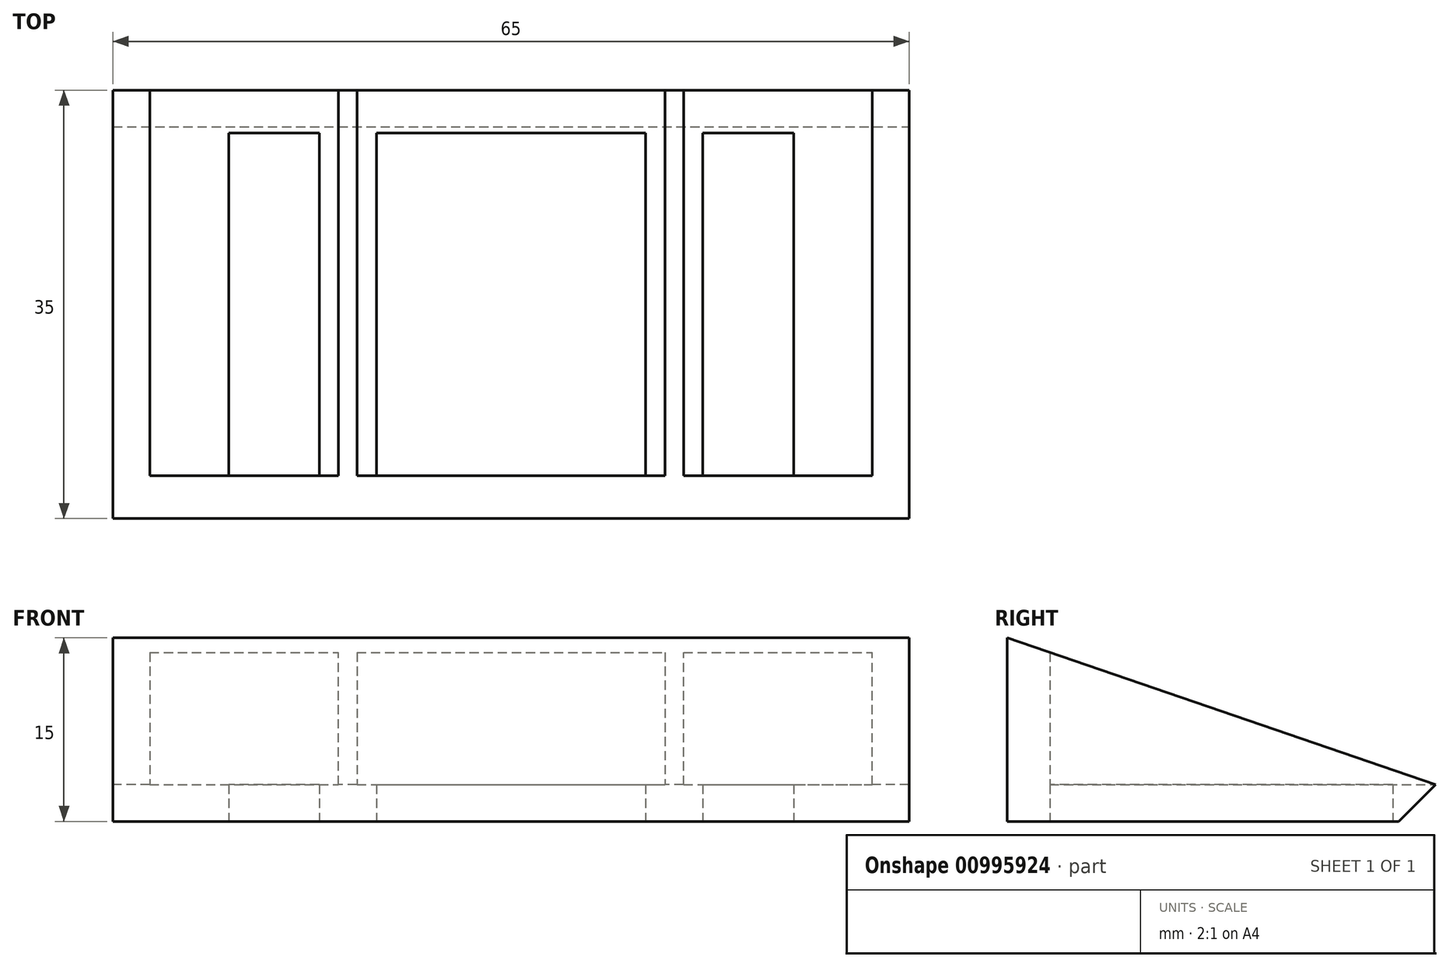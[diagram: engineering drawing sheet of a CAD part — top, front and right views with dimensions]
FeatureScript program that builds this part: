
annotation { "Feature Type Name" : "Feature", "Feature Type Description" : "" }
export const myFeature = defineFeature(function(context is Context, id is Id, definition is map)
    precondition{}
    {
        {
            var Q0;
            Q0=qCreatedBy(makeId("Top.planeOp"),FACE);
            var sketch = newSketch(context, id + "F0", { "sketchPlane" : qUnion([Q0])});
            skLineSegment(sketch, "E0.bottom", {"start": v(-32.5, 17.5) * mm, "end": v(32.5, 17.5) * mm});
            skLineSegment(sketch, "E0.top", {"start": v(-32.5, -17.5) * mm, "end": v(32.5, -17.5) * mm});
            skLineSegment(sketch, "E0.left", {"start": v(-32.5, 17.5) * mm, "end": v(-32.5, -17.5) * mm});
            skLineSegment(sketch, "E0.right", {"start": v(32.5, 17.5) * mm, "end": v(32.5, -17.5) * mm});
            skPoint(sketch, "E0.middle", {"position": v(0, 0) * mm});
            skLineSegment(sketch, "E1.left", {"start": v(-19.37, 14) * mm, "end": v(-19.37, -14) * mm, "construction": true});
            skLineSegment(sketch, "E1.right", {"start": v(19.37, 14) * mm, "end": v(19.37, -14) * mm, "construction": true});
            skLineSegment(sketch, "E2.bottom", {"start": v(-19.37, 14) * mm, "end": v(-23.07, 14) * mm});
            skLineSegment(sketch, "E2.top", {"start": v(-19.37, -14) * mm, "end": v(-23.07, -14) * mm});
            skLineSegment(sketch, "E2.left", {"start": v(-19.37, 14) * mm, "end": v(-19.37, -14) * mm});
            skLineSegment(sketch, "E2.right", {"start": v(-23.07, 14) * mm, "end": v(-23.07, -14) * mm});
            skLineSegment(sketch, "E3.MirrorCS", {"start": v(-15.67, 14) * mm, "end": v(-15.67, -14) * mm});
            skLineSegment(sketch, "E4.MirrorCS", {"start": v(-19.37, 14) * mm, "end": v(-15.67, 14) * mm});
            skLineSegment(sketch, "E5.MirrorCS", {"start": v(-19.37, -14) * mm, "end": v(-15.67, -14) * mm});
            skLineSegment(sketch, "E6.bottom", {"start": v(-11, 14) * mm, "end": v(11, 14) * mm});
            skLineSegment(sketch, "E6.top", {"start": v(-11, -14) * mm, "end": v(11, -14) * mm});
            skLineSegment(sketch, "E6.left", {"start": v(-11, 14) * mm, "end": v(-11, -14) * mm});
            skLineSegment(sketch, "E6.right", {"start": v(11, 14) * mm, "end": v(11, -14) * mm});
            skLineSegment(sketch, "E7.MirrorCS", {"start": v(15.67, 14) * mm, "end": v(15.67, -14) * mm});
            skLineSegment(sketch, "E8.MirrorCS", {"start": v(23.07, 14) * mm, "end": v(23.07, -14) * mm});
            skLineSegment(sketch, "E9.MirrorCS", {"start": v(19.37, 14) * mm, "end": v(23.07, 14) * mm});
            skLineSegment(sketch, "E10.MirrorCS", {"start": v(19.37, -14) * mm, "end": v(23.07, -14) * mm});
            skLineSegment(sketch, "E11.bottom", {"start": v(-23.07, 14) * mm, "end": v(23.07, 14) * mm});
            skLineSegment(sketch, "E11.top", {"start": v(-23.07, -14) * mm, "end": v(23.07, -14) * mm});
            skLineSegment(sketch, "E12.top", {"start": v(-32.5, -14) * mm, "end": v(32.5, -14) * mm});
            skLineSegment(sketch, "E12.left", {"start": v(-32.5, -17.5) * mm, "end": v(-32.5, -14) * mm});
            skLineSegment(sketch, "E12.right", {"start": v(32.5, -17.5) * mm, "end": v(32.5, -14) * mm});
            skLineSegment(sketch, "E13.bottom", {"start": v(-32.5, 17.5) * mm, "end": v(-29.5, 17.5) * mm});
            skLineSegment(sketch, "E13.top", {"start": v(-32.5, -17.5) * mm, "end": v(-29.5, -17.5) * mm});
            skLineSegment(sketch, "E13.right", {"start": v(-29.5, 17.5) * mm, "end": v(-29.5, -17.5) * mm});
            skLineSegment(sketch, "E14", {"start": v(-15.67, 0.77) * mm, "end": v(-11, 0.77) * mm, "construction": true});
            skLineSegment(sketch, "E15.bottom", {"start": v(-13.33, 0.77) * mm, "end": v(-12.58, 0.77) * mm});
            skLineSegment(sketch, "E15.top", {"start": v(-13.33, 17.5) * mm, "end": v(-12.58, 17.5) * mm});
            skLineSegment(sketch, "E15.left", {"start": v(-13.33, 0.77) * mm, "end": v(-13.33, 17.5) * mm});
            skLineSegment(sketch, "E15.right", {"start": v(-12.58, 0.77) * mm, "end": v(-12.58, 17.5) * mm});
            skLineSegment(sketch, "E16.MirrorCS", {"start": v(-14.08, 0.77) * mm, "end": v(-14.08, 17.5) * mm});
            skLineSegment(sketch, "E17.MirrorCS", {"start": v(-13.33, 17.5) * mm, "end": v(-14.08, 17.5) * mm});
            skLineSegment(sketch, "E18.MirrorCS", {"start": v(-11, 0.77) * mm, "end": v(-15.67, 0.77) * mm, "construction": true});
            skLineSegment(sketch, "E19.bottom", {"start": v(-14.08, 0.77) * mm, "end": v(-12.58, 0.77) * mm});
            skLineSegment(sketch, "E19.top", {"start": v(-14.08, -17.5) * mm, "end": v(-12.58, -17.5) * mm});
            skLineSegment(sketch, "E19.left", {"start": v(-14.08, 0.77) * mm, "end": v(-14.08, -17.5) * mm});
            skLineSegment(sketch, "E19.right", {"start": v(-12.58, 0.77) * mm, "end": v(-12.58, -17.5) * mm});
            skLineSegment(sketch, "E20.MirrorCS", {"start": v(12.58, 0.77) * mm, "end": v(12.58, 17.5) * mm});
            skLineSegment(sketch, "E21.MirrorCS", {"start": v(12.58, 0.77) * mm, "end": v(12.58, -17.5) * mm});
            skLineSegment(sketch, "E22.MirrorCS", {"start": v(14.08, 0.77) * mm, "end": v(14.08, -17.5) * mm});
            skLineSegment(sketch, "E23.MirrorCS", {"start": v(13.33, 17.5) * mm, "end": v(12.58, 17.5) * mm});
            skLineSegment(sketch, "E24.MirrorCS", {"start": v(13.33, 17.5) * mm, "end": v(14.08, 17.5) * mm});
            skLineSegment(sketch, "E25.MirrorCS", {"start": v(14.08, 0.77) * mm, "end": v(14.08, 17.5) * mm});
            skLineSegment(sketch, "E26.MirrorCS", {"start": v(13.33, 0.77) * mm, "end": v(13.33, 17.5) * mm});
            skLineSegment(sketch, "E27.MirrorCS", {"start": v(14.08, -17.5) * mm, "end": v(12.58, -17.5) * mm});
            skLineSegment(sketch, "E28.MirrorCS", {"start": v(29.5, 17.5) * mm, "end": v(29.5, -17.5) * mm});
            skSolve(sketch);
        }
        {
            var Q0;
            {var subQ0=sQuery(id+"F0.wireOp",EDGE,"E0.left");var subQ1=sQuery(id+"F0.wireOp",EDGE,"E0.bottom");var subQ2=makeQuery(id+"F0.imprint","INTERSECT",VERTEX,{"derivedFrom":[subQ1,subQ0]});Q0=makeQuery(id+"F0.imprint","IMPRINT",FACE,{"disambiguationData":[TD([[makeQuery(id+"F0.imprint","IMPRINT",EDGE,{"disambiguationData":[TD([[subQ2,-1.0]])],"derivedFrom":subQ1}),-1.0]])]});}
            var Q1;
            {var subQ0=sQuery(id+"F0.wireOp",EDGE,"E0.left");var subQ1=sQuery(id+"F0.wireOp",EDGE,"E0.top");var subQ2=makeQuery(id+"F0.imprint","INTERSECT",VERTEX,{"derivedFrom":[subQ1,subQ0]});Q1=makeQuery(id+"F0.imprint","IMPRINT",FACE,{"disambiguationData":[TD([[makeQuery(id+"F0.imprint","IMPRINT",EDGE,{"disambiguationData":[TD([[subQ2,-1.0]])],"derivedFrom":subQ1}),1.0]])]});}
            var Q2;
            {var subQ0=sQuery(id+"F0.wireOp",EDGE,"E19.right");var subQ1=sQuery(id+"F0.wireOp",EDGE,"E0.top");var subQ2=makeQuery(id+"F0.imprint","INTERSECT",VERTEX,{"derivedFrom":[subQ1,subQ0]});Q2=makeQuery(id+"F0.imprint","IMPRINT",FACE,{"disambiguationData":[TD([[makeQuery(id+"F0.imprint","IMPRINT",EDGE,{"disambiguationData":[TD([[subQ2,1.0]])],"derivedFrom":subQ1}),1.0]])]});}
            var Q3;
            {var subQ4=sQuery(id+"F0.wireOp",EDGE,"E15.bottom");Q3=makeQuery(id+"F0.imprint","IMPRINT",FACE,{"disambiguationData":[TD([[makeQuery(id+"F0.imprint","IMPRINT",EDGE,{"derivedFrom":subQ4}),-1.0]])]});}
            var Q4;
            {var subQ5=sQuery(id+"F0.wireOp",EDGE,"E19.bottom");Q4=makeQuery(id+"F0.imprint","IMPRINT",FACE,{"disambiguationData":[TD([[makeQuery(id+"F0.imprint","IMPRINT",EDGE,{"derivedFrom":subQ5}),1.0]])]});}
            var Q5;
            {var subQ5=sQuery(id+"F0.wireOp",EDGE,"E15.bottom");Q5=makeQuery(id+"F0.imprint","IMPRINT",FACE,{"disambiguationData":[TD([[makeQuery(id+"F0.imprint","IMPRINT",EDGE,{"derivedFrom":subQ5}),1.0]])]});}
            var Q6;
            {var subQ0=sQuery(id+"F0.wireOp",EDGE,"E15.left");var subQ1=sQuery(id+"F0.wireOp",EDGE,"E0.bottom");var subQ2=makeQuery(id+"F0.imprint","INTERSECT",VERTEX,{"derivedFrom":[subQ1,subQ0]});Q6=makeQuery(id+"F0.imprint","IMPRINT",FACE,{"disambiguationData":[TD([[makeQuery(id+"F0.imprint","IMPRINT",EDGE,{"disambiguationData":[TD([[subQ2,1.0]])],"derivedFrom":subQ1}),-1.0]])]});}
            var Q7;
            {var subQ0=sQuery(id+"F0.wireOp",EDGE,"E15.right");var subQ1=sQuery(id+"F0.wireOp",EDGE,"E0.bottom");var subQ2=makeQuery(id+"F0.imprint","INTERSECT",VERTEX,{"derivedFrom":[subQ1,subQ0]});Q7=makeQuery(id+"F0.imprint","IMPRINT",FACE,{"disambiguationData":[TD([[makeQuery(id+"F0.imprint","IMPRINT",EDGE,{"disambiguationData":[TD([[subQ2,1.0]])],"derivedFrom":subQ1}),-1.0]])]});}
            var Q8;
            {var subQ1=sQuery(id+"F0.wireOp",EDGE,"E6.top");Q8=makeQuery(id+"F0.imprint","IMPRINT",FACE,{"disambiguationData":[TD([[makeQuery(id+"F0.imprint","IMPRINT",EDGE,{"derivedFrom":subQ1}),-1.0]])]});}
            var Q9;
            {var subQ9=sQuery(id+"F0.wireOp",EDGE,"E2.top");Q9=makeQuery(id+"F0.imprint","IMPRINT",FACE,{"disambiguationData":[TD([[makeQuery(id+"F0.imprint","IMPRINT",EDGE,{"derivedFrom":subQ9}),1.0]])]});}
            var Q10;
            {var subQ0=sQuery(id+"F0.wireOp",EDGE,"E21.MirrorCS");var subQ1=sQuery(id+"F0.wireOp",EDGE,"E0.top");var subQ2=makeQuery(id+"F0.imprint","INTERSECT",VERTEX,{"derivedFrom":[subQ1,subQ0]});Q10=makeQuery(id+"F0.imprint","IMPRINT",FACE,{"disambiguationData":[TD([[makeQuery(id+"F0.imprint","IMPRINT",EDGE,{"disambiguationData":[TD([[subQ2,-1.0]])],"derivedFrom":subQ1}),1.0]])]});}
            var Q11;
            {var subQ0=sQuery(id+"F0.wireOp",EDGE,"E0.right");var subQ1=sQuery(id+"F0.wireOp",EDGE,"E0.top");var subQ2=makeQuery(id+"F0.imprint","INTERSECT",VERTEX,{"derivedFrom":[subQ1,subQ0]});Q11=makeQuery(id+"F0.imprint","IMPRINT",FACE,{"disambiguationData":[TD([[makeQuery(id+"F0.imprint","IMPRINT",EDGE,{"disambiguationData":[TD([[subQ2,1.0]])],"derivedFrom":subQ1}),1.0]])]});}
            var Q12;
            {var subQ3=sQuery(id+"F0.wireOp",EDGE,"E11.bottom");var subQ9=makeQuery(id+"F0.imprint","INTERSECT",VERTEX,{"derivedFrom":[subQ3,sQuery(id+"F0.wireOp",EDGE,"E26.MirrorCS")]});Q12=makeQuery(id+"F0.imprint","IMPRINT",FACE,{"disambiguationData":[TD([[makeQuery(id+"F0.imprint","IMPRINT",EDGE,{"disambiguationData":[TD([[subQ9,-1.0]])],"derivedFrom":subQ3}),-1.0]])]});}
            var Q13;
            {var subQ0=sQuery(id+"F0.wireOp",EDGE,"E25.MirrorCS");var subQ1=sQuery(id+"F0.wireOp",EDGE,"E0.bottom");var subQ2=makeQuery(id+"F0.imprint","INTERSECT",VERTEX,{"derivedFrom":[subQ1,subQ0]});Q13=makeQuery(id+"F0.imprint","IMPRINT",FACE,{"disambiguationData":[TD([[makeQuery(id+"F0.imprint","IMPRINT",EDGE,{"disambiguationData":[TD([[subQ2,1.0]])],"derivedFrom":subQ1}),-1.0]])]});}
            var Q14;
            {var subQ0=sQuery(id+"F0.wireOp",EDGE,"E20.MirrorCS");var subQ1=sQuery(id+"F0.wireOp",EDGE,"E0.bottom");var subQ2=makeQuery(id+"F0.imprint","INTERSECT",VERTEX,{"derivedFrom":[subQ1,subQ0]});Q14=makeQuery(id+"F0.imprint","IMPRINT",FACE,{"disambiguationData":[TD([[makeQuery(id+"F0.imprint","IMPRINT",EDGE,{"disambiguationData":[TD([[subQ2,-1.0]])],"derivedFrom":subQ1}),-1.0]])]});}
            var Q15;
            {var subQ9=sQuery(id+"F0.wireOp",EDGE,"E10.MirrorCS");Q15=makeQuery(id+"F0.imprint","IMPRINT",FACE,{"disambiguationData":[TD([[makeQuery(id+"F0.imprint","IMPRINT",EDGE,{"derivedFrom":subQ9}),-1.0]])]});}
            var Q16;
            {var subQ0=sQuery(id+"F0.wireOp",EDGE,"E0.right");var subQ1=sQuery(id+"F0.wireOp",EDGE,"E0.bottom");var subQ2=makeQuery(id+"F0.imprint","INTERSECT",VERTEX,{"derivedFrom":[subQ1,subQ0]});Q16=makeQuery(id+"F0.imprint","IMPRINT",FACE,{"disambiguationData":[TD([[makeQuery(id+"F0.imprint","IMPRINT",EDGE,{"disambiguationData":[TD([[subQ2,1.0]])],"derivedFrom":subQ1}),-1.0]])]});}
            extrude(context, id + "F1", {"entities" : qUnion([Q0, Q1, Q2, Q3, Q4, Q5, Q6, Q7, Q8, Q9, Q10, Q11, Q12, Q13, Q14, Q15, Q16]), "depth" : 15 * mm, "offsetDistance" : 25 * mm});
        }
        {
            var Q0;
            Q0=makeQuery(id+"F0.imprint","IMPRINT",FACE,{"disambiguationData":[TD([[makeQuery(id+"F0.imprint","IMPRINT",EDGE,{"derivedFrom":sQuery(id+"F0.wireOp",EDGE,"E2.bottom")}),-1.0]])]});
            var Q1;
            {var subQ1=sQuery(id+"F0.wireOp",EDGE,"E3.MirrorCS");Q1=makeQuery(id+"F0.imprint","IMPRINT",FACE,{"disambiguationData":[TD([[makeQuery(id+"F0.imprint","IMPRINT",EDGE,{"derivedFrom":subQ1}),1.0]])]});}
            var Q2;
            {var subQ6=sQuery(id+"F0.wireOp",EDGE,"E6.left");Q2=makeQuery(id+"F0.imprint","IMPRINT",FACE,{"disambiguationData":[TD([[makeQuery(id+"F0.imprint","IMPRINT",EDGE,{"derivedFrom":subQ6}),-1.0]])]});}
            var Q3;
            {var subQ1=sQuery(id+"F0.wireOp",EDGE,"E6.bottom");Q3=makeQuery(id+"F0.imprint","IMPRINT",FACE,{"disambiguationData":[TD([[makeQuery(id+"F0.imprint","IMPRINT",EDGE,{"derivedFrom":subQ1}),1.0]])]});}
            var Q4;
            {var subQ0=sQuery(id+"F0.wireOp",EDGE,"E15.left");var subQ1=sQuery(id+"F0.wireOp",EDGE,"E0.bottom");var subQ2=makeQuery(id+"F0.imprint","INTERSECT",VERTEX,{"derivedFrom":[subQ1,subQ0]});Q4=makeQuery(id+"F0.imprint","IMPRINT",FACE,{"disambiguationData":[TD([[makeQuery(id+"F0.imprint","IMPRINT",EDGE,{"disambiguationData":[TD([[subQ2,1.0]])],"derivedFrom":subQ1}),-1.0]])]});}
            var Q5;
            {var subQ0=sQuery(id+"F0.wireOp",EDGE,"E15.right");var subQ1=sQuery(id+"F0.wireOp",EDGE,"E0.bottom");var subQ2=makeQuery(id+"F0.imprint","INTERSECT",VERTEX,{"derivedFrom":[subQ1,subQ0]});Q5=makeQuery(id+"F0.imprint","IMPRINT",FACE,{"disambiguationData":[TD([[makeQuery(id+"F0.imprint","IMPRINT",EDGE,{"disambiguationData":[TD([[subQ2,1.0]])],"derivedFrom":subQ1}),-1.0]])]});}
            var Q6;
            {var subQ8=sQuery(id+"F0.wireOp",EDGE,"E8.MirrorCS");Q6=makeQuery(id+"F0.imprint","IMPRINT",FACE,{"disambiguationData":[TD([[makeQuery(id+"F0.imprint","IMPRINT",EDGE,{"derivedFrom":subQ8}),1.0]])]});}
            var Q7;
            {var subQ1=sQuery(id+"F0.wireOp",EDGE,"E6.right");Q7=makeQuery(id+"F0.imprint","IMPRINT",FACE,{"disambiguationData":[TD([[makeQuery(id+"F0.imprint","IMPRINT",EDGE,{"derivedFrom":subQ1}),1.0]])]});}
            var Q8;
            {var subQ6=sQuery(id+"F0.wireOp",EDGE,"E7.MirrorCS");Q8=makeQuery(id+"F0.imprint","IMPRINT",FACE,{"disambiguationData":[TD([[makeQuery(id+"F0.imprint","IMPRINT",EDGE,{"derivedFrom":subQ6}),-1.0]])]});}
            extrude(context, id + "F2", {"entities" : qUnion([Q0, Q1, Q2, Q3, Q4, Q5, Q6, Q7, Q8]), "operationType" : NewBodyOperationType.ADD, "depth" : 3 * mm, "offsetDistance" : 25 * mm});
        }
        {
            var Q0;
            {var subQ0=sQuery(id+"F0.wireOp",EDGE,"E0.bottom");var subQ1=makeQuery(id+"F0.imprint","INTERSECT",VERTEX,{"derivedFrom":[subQ0,sQuery(id+"F0.wireOp",EDGE,"E25.MirrorCS")]});var subQ3=makeQuery(id+"F0.imprint","INTERSECT",VERTEX,{"derivedFrom":[subQ0,sQuery(id+"F0.wireOp",EDGE,"E15.left")]});var subQ5=makeQuery(id+"F0.imprint","IMPRINT",EDGE,{"disambiguationData":[TD([[subQ3,1.0]])],"derivedFrom":subQ0});var subQ6=makeQuery(id+"F0.imprint","INTERSECT",VERTEX,{"derivedFrom":[subQ0,sQuery(id+"F0.wireOp",EDGE,"E15.right")]});var subQ7=makeQuery(id+"F0.imprint","IMPRINT",EDGE,{"disambiguationData":[TD([[subQ6,1.0]])],"derivedFrom":subQ0});var subQ8=makeQuery(id+"F0.imprint","INTERSECT",VERTEX,{"derivedFrom":[subQ0,sQuery(id+"F0.wireOp",EDGE,"E13.right")]});var subQ9=makeQuery(id+"F0.imprint","INTERSECT",VERTEX,{"derivedFrom":[subQ0,sQuery(id+"F0.wireOp",EDGE,"E20.MirrorCS")]});Q0=makeQuery(id+"F2.boolean.opBoolean","MERGE",EDGE,{"derivedFrom":[makeQuery(id+"F1.opExtrude","CAP_EDGE",EDGE,{"disambiguationData":[OSD([subQ0]),TDD([makeQuery(id+"F0.imprint","IMPRINT",EDGE,{"disambiguationData":[TD([[makeQuery(id+"F0.imprint","INTERSECT",VERTEX,{"derivedFrom":[subQ0,sQuery(id+"F0.wireOp",EDGE,"E0.left")]}),-1.0]])],"derivedFrom":subQ0})])],"isStart":true}),makeQuery(id+"F1.opExtrude","CAP_EDGE",EDGE,{"disambiguationData":[OSD([subQ0]),TDD([makeQuery(id+"F0.imprint","IMPRINT",EDGE,{"disambiguationData":[TD([[makeQuery(id+"F0.imprint","INTERSECT",VERTEX,{"derivedFrom":[subQ0,sQuery(id+"F0.wireOp",EDGE,"E0.right")]}),1.0]])],"derivedFrom":subQ0})])],"isStart":true}),makeQuery(id+"F1.opExtrude","CAP_EDGE",EDGE,{"disambiguationData":[OSD([subQ0]),TDD([subQ7,subQ5])],"isStart":true}),makeQuery(id+"F1.opExtrude","CAP_EDGE",EDGE,{"disambiguationData":[OSD([subQ0]),TDD([makeQuery(id+"F0.imprint","IMPRINT",EDGE,{"disambiguationData":[TD([[subQ1,1.0]])],"derivedFrom":subQ0}),makeQuery(id+"F0.imprint","IMPRINT",EDGE,{"disambiguationData":[TD([[subQ9,-1.0]])],"derivedFrom":subQ0})])],"isStart":true}),makeQuery(id+"F2.opExtrude","CAP_EDGE",EDGE,{"disambiguationData":[OSD([subQ0]),TDD([makeQuery(id+"F0.imprint","IMPRINT",EDGE,{"disambiguationData":[TD([[subQ6,-1.0]])],"derivedFrom":subQ0}),makeQuery(id+"F0.imprint","IMPRINT",EDGE,{"disambiguationData":[TD([[subQ8,-1.0]])],"derivedFrom":subQ0}),subQ7,subQ5])],"isStart":true}),makeQuery(id+"F2.opExtrude","CAP_EDGE",EDGE,{"disambiguationData":[OSD([subQ0]),TDD([makeQuery(id+"F0.imprint","IMPRINT",EDGE,{"disambiguationData":[TD([[subQ1,-1.0]])],"derivedFrom":subQ0})])],"isStart":true})]});}
            chamfer(context, id + "F3", {"entities" : qUnion([Q0]), "width" : 3 * mm, "tangentPropagation" : true});
        }
        {
            var Q0;
            Q0=makeQuery(id+"F1.opExtrude","SWEPT_FACE",FACE,{"disambiguationData":[OSD([sQuery(id+"F0.wireOp",EDGE,"E0.right")])]});
            var sketch = newSketch(context, id + "F4", { "sketchPlane" : qUnion([Q0])});
            skLineSegment(sketch, "E29", {"start": v(17.5, 3) * mm, "end": v(-17.5, 15) * mm});
            skLineSegment(sketch, "E30", {"start": v(-17.5, 15) * mm, "end": v(17.5, 15) * mm});
            skLineSegment(sketch, "E31", {"start": v(17.5, 15) * mm, "end": v(17.5, 3) * mm});
            skSolve(sketch);
        }
        {
            var Q0;
            Q0=makeQuery(id+"F4.imprint","IMPRINT",FACE,{"disambiguationData":[TD([[makeQuery(id+"F4.imprint","IMPRINT",EDGE,{"derivedFrom":sQuery(id+"F4.wireOp",EDGE,"E29")}),-1.0]])]});
            extrude(context, id + "F5", {"entities" : qUnion([Q0]), "operationType" : NewBodyOperationType.REMOVE, "oppositeDirection" : true, "depth" : 83.7 * mm, "offsetDistance" : 25 * mm});
        }
    });
